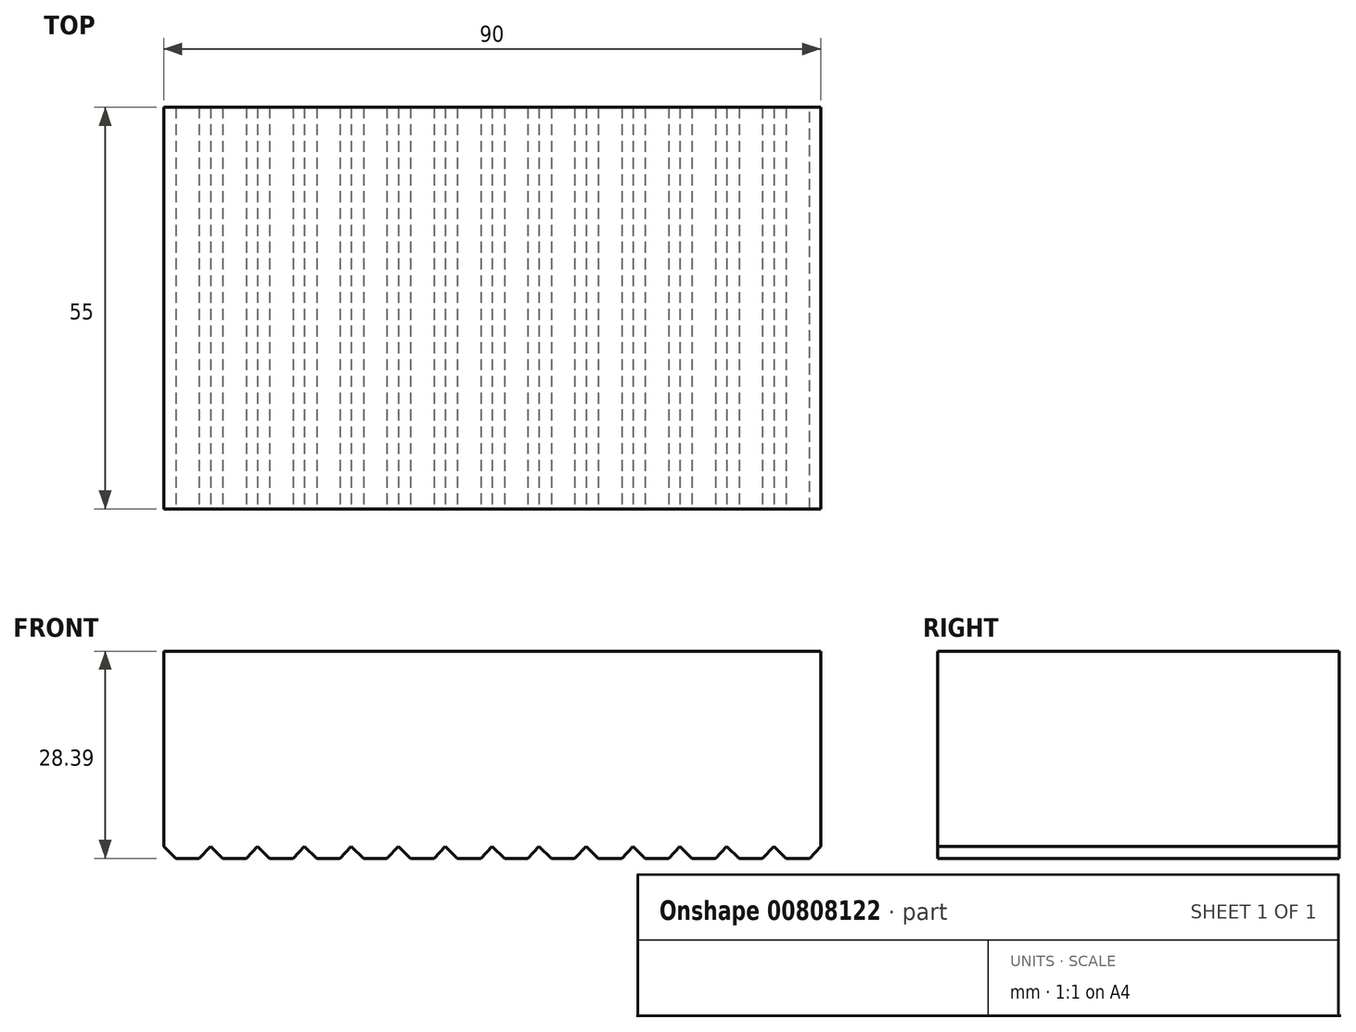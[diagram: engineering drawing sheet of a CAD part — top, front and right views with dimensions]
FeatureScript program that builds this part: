
annotation { "Feature Type Name" : "Feature", "Feature Type Description" : "" }
export const myFeature = defineFeature(function(context is Context, id is Id, definition is map)
    precondition{}
    {
        {
            var Q0;
            Q0=qCreatedBy(makeId("Top.planeOp"),FACE);
            var sketch = newSketch(context, id + "F0", { "sketchPlane" : qUnion([Q0])});
            skLineSegment(sketch, "E0.bottom", {"start": v(0, 0) * mm, "end": v(90, 0) * mm});
            skLineSegment(sketch, "E0.top", {"start": v(0, -55) * mm, "end": v(90, -55) * mm});
            skLineSegment(sketch, "E0.left", {"start": v(0, 0) * mm, "end": v(0, -55) * mm});
            skLineSegment(sketch, "E0.right", {"start": v(90, 0) * mm, "end": v(90, -55) * mm});
            skSolve(sketch);
        }
        {
            var Q0;
            Q0 = qSketchRegion(id + "F0", true);
            extrude(context, id + "F1", {"entities" : qUnion([Q0]), "depth" : 30 * mm, "offsetDistance" : 25 * mm});
        }
        {
            var Q0;
            Q0=makeQuery(id+"F1.opExtrude","SWEPT_FACE",FACE,{"disambiguationData":[OSD([sQuery(id+"F0.wireOp",EDGE,"E0.top")])]});
            var sketch = newSketch(context, id + "F2", { "sketchPlane" : qUnion([Q0])});
            skLineSegment(sketch, "E1", {"start": v(0, 3.21) * mm, "end": v(3.35, 0) * mm});
            skLineSegment(sketch, "E2", {"start": v(3.35, 0) * mm, "end": v(6.43, 3.21) * mm});
            skLineSegment(sketch, "E3", {"start": v(6.43, 3.21) * mm, "end": v(9.77, 0) * mm});
            skLineSegment(sketch, "E4", {"start": v(9.77, 0) * mm, "end": v(12.86, 3.21) * mm});
            skLineSegment(sketch, "E5", {"start": v(12.86, 3.21) * mm, "end": v(16.2, 0) * mm});
            skLineSegment(sketch, "E6", {"start": v(16.2, 0) * mm, "end": v(19.29, 3.21) * mm});
            skLineSegment(sketch, "E7", {"start": v(19.29, 3.21) * mm, "end": v(22.63, 0) * mm});
            skLineSegment(sketch, "E8", {"start": v(22.63, 0) * mm, "end": v(25.71, 3.21) * mm});
            skLineSegment(sketch, "E9", {"start": v(25.71, 3.21) * mm, "end": v(29.06, 0) * mm});
            skLineSegment(sketch, "E10", {"start": v(29.06, 0) * mm, "end": v(32.14, 3.21) * mm});
            skLineSegment(sketch, "E11", {"start": v(32.14, 3.21) * mm, "end": v(35.49, 0) * mm});
            skLineSegment(sketch, "E12", {"start": v(35.49, 0) * mm, "end": v(38.57, 3.21) * mm});
            skLineSegment(sketch, "E13", {"start": v(38.57, 3.21) * mm, "end": v(41.92, 0) * mm});
            skLineSegment(sketch, "E14", {"start": v(41.92, 0) * mm, "end": v(45, 3.21) * mm});
            skLineSegment(sketch, "E15", {"start": v(45, 3.21) * mm, "end": v(48.35, 0) * mm});
            skLineSegment(sketch, "E16", {"start": v(48.35, 0) * mm, "end": v(51.43, 3.21) * mm});
            skLineSegment(sketch, "E17", {"start": v(51.43, 3.21) * mm, "end": v(54.77, 0) * mm});
            skLineSegment(sketch, "E18", {"start": v(54.77, 0) * mm, "end": v(57.86, 3.21) * mm});
            skLineSegment(sketch, "E19", {"start": v(57.86, 3.21) * mm, "end": v(61.2, 0) * mm});
            skLineSegment(sketch, "E20", {"start": v(61.2, 0) * mm, "end": v(64.29, 3.21) * mm});
            skLineSegment(sketch, "E21", {"start": v(64.29, 3.21) * mm, "end": v(67.63, 0) * mm});
            skLineSegment(sketch, "E22", {"start": v(67.63, 0) * mm, "end": v(70.71, 3.21) * mm});
            skLineSegment(sketch, "E23", {"start": v(70.71, 3.21) * mm, "end": v(74.06, 0) * mm});
            skLineSegment(sketch, "E24", {"start": v(74.06, 0) * mm, "end": v(77.14, 3.21) * mm});
            skLineSegment(sketch, "E25", {"start": v(77.14, 3.21) * mm, "end": v(80.49, 0) * mm});
            skLineSegment(sketch, "E26", {"start": v(80.49, 0) * mm, "end": v(83.57, 3.21) * mm});
            skLineSegment(sketch, "E27", {"start": v(83.57, 3.21) * mm, "end": v(86.92, 0) * mm});
            skLineSegment(sketch, "E28", {"start": v(86.92, 0) * mm, "end": v(90, 3.21) * mm});
            skLineSegment(sketch, "E29", {"start": v(0, 3.21) * mm, "end": v(90, 3.21) * mm});
            skSolve(sketch);
        }
        {
            var Q0;
            {var subQ0=sQuery(id+"F2.wireOp",EDGE,"E1");Q0=makeQuery(id+"F2.imprint","IMPRINT",FACE,{"disambiguationData":[TD([[makeQuery(id+"F2.imprint","IMPRINT",EDGE,{"derivedFrom":subQ0}),-1.0]])]});}
            var Q1;
            {var subQ0=sQuery(id+"F2.wireOp",EDGE,"E2");Q1=makeQuery(id+"F2.imprint","IMPRINT",FACE,{"disambiguationData":[TD([[makeQuery(id+"F2.imprint","IMPRINT",EDGE,{"derivedFrom":subQ0}),-1.0]])]});}
            var Q2;
            {var subQ0=sQuery(id+"F2.wireOp",EDGE,"E4");Q2=makeQuery(id+"F2.imprint","IMPRINT",FACE,{"disambiguationData":[TD([[makeQuery(id+"F2.imprint","IMPRINT",EDGE,{"derivedFrom":subQ0}),-1.0]])]});}
            var Q3;
            {var subQ0=sQuery(id+"F2.wireOp",EDGE,"E6");Q3=makeQuery(id+"F2.imprint","IMPRINT",FACE,{"disambiguationData":[TD([[makeQuery(id+"F2.imprint","IMPRINT",EDGE,{"derivedFrom":subQ0}),-1.0]])]});}
            var Q4;
            {var subQ0=sQuery(id+"F2.wireOp",EDGE,"E8");Q4=makeQuery(id+"F2.imprint","IMPRINT",FACE,{"disambiguationData":[TD([[makeQuery(id+"F2.imprint","IMPRINT",EDGE,{"derivedFrom":subQ0}),-1.0]])]});}
            var Q5;
            {var subQ0=sQuery(id+"F2.wireOp",EDGE,"E10");Q5=makeQuery(id+"F2.imprint","IMPRINT",FACE,{"disambiguationData":[TD([[makeQuery(id+"F2.imprint","IMPRINT",EDGE,{"derivedFrom":subQ0}),-1.0]])]});}
            var Q6;
            {var subQ0=sQuery(id+"F2.wireOp",EDGE,"E12");Q6=makeQuery(id+"F2.imprint","IMPRINT",FACE,{"disambiguationData":[TD([[makeQuery(id+"F2.imprint","IMPRINT",EDGE,{"derivedFrom":subQ0}),-1.0]])]});}
            var Q7;
            {var subQ0=sQuery(id+"F2.wireOp",EDGE,"E14");Q7=makeQuery(id+"F2.imprint","IMPRINT",FACE,{"disambiguationData":[TD([[makeQuery(id+"F2.imprint","IMPRINT",EDGE,{"derivedFrom":subQ0}),-1.0]])]});}
            var Q8;
            {var subQ0=sQuery(id+"F2.wireOp",EDGE,"E16");Q8=makeQuery(id+"F2.imprint","IMPRINT",FACE,{"disambiguationData":[TD([[makeQuery(id+"F2.imprint","IMPRINT",EDGE,{"derivedFrom":subQ0}),-1.0]])]});}
            var Q9;
            {var subQ0=sQuery(id+"F2.wireOp",EDGE,"E18");Q9=makeQuery(id+"F2.imprint","IMPRINT",FACE,{"disambiguationData":[TD([[makeQuery(id+"F2.imprint","IMPRINT",EDGE,{"derivedFrom":subQ0}),-1.0]])]});}
            var Q10;
            {var subQ0=sQuery(id+"F2.wireOp",EDGE,"E20");Q10=makeQuery(id+"F2.imprint","IMPRINT",FACE,{"disambiguationData":[TD([[makeQuery(id+"F2.imprint","IMPRINT",EDGE,{"derivedFrom":subQ0}),-1.0]])]});}
            var Q11;
            {var subQ0=sQuery(id+"F2.wireOp",EDGE,"E22");Q11=makeQuery(id+"F2.imprint","IMPRINT",FACE,{"disambiguationData":[TD([[makeQuery(id+"F2.imprint","IMPRINT",EDGE,{"derivedFrom":subQ0}),-1.0]])]});}
            var Q12;
            {var subQ0=sQuery(id+"F2.wireOp",EDGE,"E24");Q12=makeQuery(id+"F2.imprint","IMPRINT",FACE,{"disambiguationData":[TD([[makeQuery(id+"F2.imprint","IMPRINT",EDGE,{"derivedFrom":subQ0}),-1.0]])]});}
            var Q13;
            {var subQ0=sQuery(id+"F2.wireOp",EDGE,"E26");Q13=makeQuery(id+"F2.imprint","IMPRINT",FACE,{"disambiguationData":[TD([[makeQuery(id+"F2.imprint","IMPRINT",EDGE,{"derivedFrom":subQ0}),-1.0]])]});}
            var Q14;
            {var subQ0=sQuery(id+"F2.wireOp",EDGE,"E28");Q14=makeQuery(id+"F2.imprint","IMPRINT",FACE,{"disambiguationData":[TD([[makeQuery(id+"F2.imprint","IMPRINT",EDGE,{"derivedFrom":subQ0}),-1.0]])]});}
            extrude(context, id + "F3", {"entities" : qUnion([Q0, Q1, Q2, Q3, Q4, Q5, Q6, Q7, Q8, Q9, Q10, Q11, Q12, Q13, Q14]), "operationType" : NewBodyOperationType.REMOVE, "oppositeDirection" : true, "depth" : 90 * mm, "offsetDistance" : 25 * mm});
        }
        {
            var Q0;
            Q0=makeQuery(id+"F1.opExtrude","SWEPT_FACE",FACE,{"disambiguationData":[OSD([sQuery(id+"F0.wireOp",EDGE,"E0.top")])]});
            var sketch = newSketch(context, id + "F4", { "sketchPlane" : qUnion([Q0])});
            skPoint(sketch, "E30.oppositeSnap0", {"position": v(88.46, 1.6) * mm});
            skLineSegment(sketch, "E30.bottom", {"start": v(0, 0) * mm, "end": v(90, 0) * mm});
            skLineSegment(sketch, "E30.top", {"start": v(0, 1.6) * mm, "end": v(90, 1.6) * mm});
            skLineSegment(sketch, "E30.left", {"start": v(0, 0) * mm, "end": v(0, 1.6) * mm});
            skLineSegment(sketch, "E30.right", {"start": v(90, 0) * mm, "end": v(90, 1.6) * mm});
            skSolve(sketch);
        }
        {
            var Q0;
            {var subQ3=sQuery(id+"F4.wireOp",EDGE,"E30.left");Q0=makeQuery(id+"F4.imprint","IMPRINT",FACE,{"disambiguationData":[TD([[makeQuery(id+"F4.imprint","IMPRINT",EDGE,{"derivedFrom":subQ3}),-1.0]])]});}
            var Q1;
            {var subQ3=sQuery(id+"F4.wireOp",EDGE,"E30.right");Q1=makeQuery(id+"F4.imprint","IMPRINT",FACE,{"disambiguationData":[TD([[makeQuery(id+"F4.imprint","IMPRINT",EDGE,{"derivedFrom":subQ3}),1.0]])]});}
            var Q2;
            {var subQ1=makeQuery(id+"F3.boolean.opBoolean","COPY",EDGE,{"derivedFrom":makeQuery(id+"F3.opExtrude","CAP_EDGE",EDGE,{"disambiguationData":[OSD([sQuery(id+"F2.wireOp",EDGE,"E2")])],"isStart":true})});var subQ5=sQuery(id+"F4.wireOp",EDGE,"E30.top");var subQ6=makeQuery(id+"F4.imprint","INTERSECT",VERTEX,{"derivedFrom":[subQ1,subQ5]});Q2=makeQuery(id+"F4.imprint","IMPRINT",FACE,{"disambiguationData":[TD([[makeQuery(id+"F4.imprint","IMPRINT",EDGE,{"disambiguationData":[TD([[subQ6,-1.0]])],"derivedFrom":subQ5}),-1.0]])]});}
            var Q3;
            {var subQ1=makeQuery(id+"F3.boolean.opBoolean","COPY",EDGE,{"derivedFrom":makeQuery(id+"F3.opExtrude","CAP_EDGE",EDGE,{"disambiguationData":[OSD([sQuery(id+"F2.wireOp",EDGE,"E4")])],"isStart":true})});var subQ5=sQuery(id+"F4.wireOp",EDGE,"E30.top");var subQ7=makeQuery(id+"F4.imprint","INTERSECT",VERTEX,{"derivedFrom":[subQ1,subQ5]});Q3=makeQuery(id+"F4.imprint","IMPRINT",FACE,{"disambiguationData":[TD([[makeQuery(id+"F4.imprint","IMPRINT",EDGE,{"disambiguationData":[TD([[subQ7,-1.0]])],"derivedFrom":subQ5}),-1.0]])]});}
            var Q4;
            {var subQ1=makeQuery(id+"F3.boolean.opBoolean","COPY",EDGE,{"derivedFrom":makeQuery(id+"F3.opExtrude","CAP_EDGE",EDGE,{"disambiguationData":[OSD([sQuery(id+"F2.wireOp",EDGE,"E8")])],"isStart":true})});var subQ5=sQuery(id+"F4.wireOp",EDGE,"E30.top");var subQ6=makeQuery(id+"F4.imprint","INTERSECT",VERTEX,{"derivedFrom":[subQ1,subQ5]});Q4=makeQuery(id+"F4.imprint","IMPRINT",FACE,{"disambiguationData":[TD([[makeQuery(id+"F4.imprint","IMPRINT",EDGE,{"disambiguationData":[TD([[subQ6,-1.0]])],"derivedFrom":subQ5}),-1.0]])]});}
            var Q5;
            {var subQ1=makeQuery(id+"F3.boolean.opBoolean","COPY",EDGE,{"derivedFrom":makeQuery(id+"F3.opExtrude","CAP_EDGE",EDGE,{"disambiguationData":[OSD([sQuery(id+"F2.wireOp",EDGE,"E10")])],"isStart":true})});var subQ5=sQuery(id+"F4.wireOp",EDGE,"E30.top");var subQ6=makeQuery(id+"F4.imprint","INTERSECT",VERTEX,{"derivedFrom":[subQ1,subQ5]});Q5=makeQuery(id+"F4.imprint","IMPRINT",FACE,{"disambiguationData":[TD([[makeQuery(id+"F4.imprint","IMPRINT",EDGE,{"disambiguationData":[TD([[subQ6,-1.0]])],"derivedFrom":subQ5}),-1.0]])]});}
            var Q6;
            {var subQ1=makeQuery(id+"F3.boolean.opBoolean","COPY",EDGE,{"derivedFrom":makeQuery(id+"F3.opExtrude","CAP_EDGE",EDGE,{"disambiguationData":[OSD([sQuery(id+"F2.wireOp",EDGE,"E12")])],"isStart":true})});var subQ5=sQuery(id+"F4.wireOp",EDGE,"E30.top");var subQ6=makeQuery(id+"F4.imprint","INTERSECT",VERTEX,{"derivedFrom":[subQ1,subQ5]});Q6=makeQuery(id+"F4.imprint","IMPRINT",FACE,{"disambiguationData":[TD([[makeQuery(id+"F4.imprint","IMPRINT",EDGE,{"disambiguationData":[TD([[subQ6,-1.0]])],"derivedFrom":subQ5}),-1.0]])]});}
            var Q7;
            {var subQ1=makeQuery(id+"F3.boolean.opBoolean","COPY",EDGE,{"derivedFrom":makeQuery(id+"F3.opExtrude","CAP_EDGE",EDGE,{"disambiguationData":[OSD([sQuery(id+"F2.wireOp",EDGE,"E14")])],"isStart":true})});var subQ5=sQuery(id+"F4.wireOp",EDGE,"E30.top");var subQ7=makeQuery(id+"F4.imprint","INTERSECT",VERTEX,{"derivedFrom":[subQ1,subQ5]});Q7=makeQuery(id+"F4.imprint","IMPRINT",FACE,{"disambiguationData":[TD([[makeQuery(id+"F4.imprint","IMPRINT",EDGE,{"disambiguationData":[TD([[subQ7,-1.0]])],"derivedFrom":subQ5}),-1.0]])]});}
            var Q8;
            {var subQ1=makeQuery(id+"F3.boolean.opBoolean","COPY",EDGE,{"derivedFrom":makeQuery(id+"F3.opExtrude","CAP_EDGE",EDGE,{"disambiguationData":[OSD([sQuery(id+"F2.wireOp",EDGE,"E16")])],"isStart":true})});var subQ5=sQuery(id+"F4.wireOp",EDGE,"E30.top");var subQ6=makeQuery(id+"F4.imprint","INTERSECT",VERTEX,{"derivedFrom":[subQ1,subQ5]});Q8=makeQuery(id+"F4.imprint","IMPRINT",FACE,{"disambiguationData":[TD([[makeQuery(id+"F4.imprint","IMPRINT",EDGE,{"disambiguationData":[TD([[subQ6,-1.0]])],"derivedFrom":subQ5}),-1.0]])]});}
            var Q9;
            {var subQ1=makeQuery(id+"F3.boolean.opBoolean","COPY",EDGE,{"derivedFrom":makeQuery(id+"F3.opExtrude","CAP_EDGE",EDGE,{"disambiguationData":[OSD([sQuery(id+"F2.wireOp",EDGE,"E18")])],"isStart":true})});var subQ5=sQuery(id+"F4.wireOp",EDGE,"E30.top");var subQ6=makeQuery(id+"F4.imprint","INTERSECT",VERTEX,{"derivedFrom":[subQ1,subQ5]});Q9=makeQuery(id+"F4.imprint","IMPRINT",FACE,{"disambiguationData":[TD([[makeQuery(id+"F4.imprint","IMPRINT",EDGE,{"disambiguationData":[TD([[subQ6,-1.0]])],"derivedFrom":subQ5}),-1.0]])]});}
            var Q10;
            {var subQ1=makeQuery(id+"F3.boolean.opBoolean","COPY",EDGE,{"derivedFrom":makeQuery(id+"F3.opExtrude","CAP_EDGE",EDGE,{"disambiguationData":[OSD([sQuery(id+"F2.wireOp",EDGE,"E20")])],"isStart":true})});var subQ5=sQuery(id+"F4.wireOp",EDGE,"E30.top");var subQ6=makeQuery(id+"F4.imprint","INTERSECT",VERTEX,{"derivedFrom":[subQ1,subQ5]});Q10=makeQuery(id+"F4.imprint","IMPRINT",FACE,{"disambiguationData":[TD([[makeQuery(id+"F4.imprint","IMPRINT",EDGE,{"disambiguationData":[TD([[subQ6,-1.0]])],"derivedFrom":subQ5}),-1.0]])]});}
            var Q11;
            {var subQ1=makeQuery(id+"F3.boolean.opBoolean","COPY",EDGE,{"derivedFrom":makeQuery(id+"F3.opExtrude","CAP_EDGE",EDGE,{"disambiguationData":[OSD([sQuery(id+"F2.wireOp",EDGE,"E22")])],"isStart":true})});var subQ5=sQuery(id+"F4.wireOp",EDGE,"E30.top");var subQ6=makeQuery(id+"F4.imprint","INTERSECT",VERTEX,{"derivedFrom":[subQ1,subQ5]});Q11=makeQuery(id+"F4.imprint","IMPRINT",FACE,{"disambiguationData":[TD([[makeQuery(id+"F4.imprint","IMPRINT",EDGE,{"disambiguationData":[TD([[subQ6,-1.0]])],"derivedFrom":subQ5}),-1.0]])]});}
            var Q12;
            {var subQ1=makeQuery(id+"F3.boolean.opBoolean","COPY",EDGE,{"derivedFrom":makeQuery(id+"F3.opExtrude","CAP_EDGE",EDGE,{"disambiguationData":[OSD([sQuery(id+"F2.wireOp",EDGE,"E24")])],"isStart":true})});var subQ5=sQuery(id+"F4.wireOp",EDGE,"E30.top");var subQ7=makeQuery(id+"F4.imprint","INTERSECT",VERTEX,{"derivedFrom":[subQ1,subQ5]});Q12=makeQuery(id+"F4.imprint","IMPRINT",FACE,{"disambiguationData":[TD([[makeQuery(id+"F4.imprint","IMPRINT",EDGE,{"disambiguationData":[TD([[subQ7,-1.0]])],"derivedFrom":subQ5}),-1.0]])]});}
            var Q13;
            {var subQ1=makeQuery(id+"F3.boolean.opBoolean","COPY",EDGE,{"derivedFrom":makeQuery(id+"F3.opExtrude","CAP_EDGE",EDGE,{"disambiguationData":[OSD([sQuery(id+"F2.wireOp",EDGE,"E26")])],"isStart":true})});var subQ5=sQuery(id+"F4.wireOp",EDGE,"E30.top");var subQ6=makeQuery(id+"F4.imprint","INTERSECT",VERTEX,{"derivedFrom":[subQ1,subQ5]});Q13=makeQuery(id+"F4.imprint","IMPRINT",FACE,{"disambiguationData":[TD([[makeQuery(id+"F4.imprint","IMPRINT",EDGE,{"disambiguationData":[TD([[subQ6,-1.0]])],"derivedFrom":subQ5}),-1.0]])]});}
            var Q14;
            {var subQ0=sQuery(id+"F4.wireOp",EDGE,"E30.top");var subQ1=makeQuery(id+"F3.boolean.opBoolean","COPY",EDGE,{"derivedFrom":makeQuery(id+"F3.opExtrude","CAP_EDGE",EDGE,{"disambiguationData":[OSD([sQuery(id+"F2.wireOp",EDGE,"E1")])],"isStart":true})});var subQ2=makeQuery(id+"F4.imprint","INTERSECT",VERTEX,{"derivedFrom":[subQ1,subQ0]});Q14=makeQuery(id+"F4.imprint","IMPRINT",FACE,{"disambiguationData":[TD([[makeQuery(id+"F4.imprint","IMPRINT",EDGE,{"disambiguationData":[TD([[subQ2,-1.0]])],"derivedFrom":subQ0}),-1.0]])]});}
            var Q15;
            {var subQ0=sQuery(id+"F4.wireOp",EDGE,"E30.top");var subQ1=makeQuery(id+"F3.boolean.opBoolean","COPY",EDGE,{"derivedFrom":makeQuery(id+"F3.opExtrude","CAP_EDGE",EDGE,{"disambiguationData":[OSD([sQuery(id+"F2.wireOp",EDGE,"E3")])],"isStart":true})});var subQ2=makeQuery(id+"F4.imprint","INTERSECT",VERTEX,{"derivedFrom":[subQ1,subQ0]});Q15=makeQuery(id+"F4.imprint","IMPRINT",FACE,{"disambiguationData":[TD([[makeQuery(id+"F4.imprint","IMPRINT",EDGE,{"disambiguationData":[TD([[subQ2,-1.0]])],"derivedFrom":subQ0}),-1.0]])]});}
            var Q16;
            {var subQ0=sQuery(id+"F4.wireOp",EDGE,"E30.top");var subQ1=makeQuery(id+"F3.boolean.opBoolean","COPY",EDGE,{"derivedFrom":makeQuery(id+"F3.opExtrude","CAP_EDGE",EDGE,{"disambiguationData":[OSD([sQuery(id+"F2.wireOp",EDGE,"E5")])],"isStart":true})});var subQ2=makeQuery(id+"F4.imprint","INTERSECT",VERTEX,{"derivedFrom":[subQ1,subQ0]});Q16=makeQuery(id+"F4.imprint","IMPRINT",FACE,{"disambiguationData":[TD([[makeQuery(id+"F4.imprint","IMPRINT",EDGE,{"disambiguationData":[TD([[subQ2,-1.0]])],"derivedFrom":subQ0}),-1.0]])]});}
            var Q17;
            {var subQ0=sQuery(id+"F4.wireOp",EDGE,"E30.top");var subQ1=makeQuery(id+"F3.boolean.opBoolean","COPY",EDGE,{"derivedFrom":makeQuery(id+"F3.opExtrude","CAP_EDGE",EDGE,{"disambiguationData":[OSD([sQuery(id+"F2.wireOp",EDGE,"E7")])],"isStart":true})});var subQ2=makeQuery(id+"F4.imprint","INTERSECT",VERTEX,{"derivedFrom":[subQ1,subQ0]});Q17=makeQuery(id+"F4.imprint","IMPRINT",FACE,{"disambiguationData":[TD([[makeQuery(id+"F4.imprint","IMPRINT",EDGE,{"disambiguationData":[TD([[subQ2,-1.0]])],"derivedFrom":subQ0}),-1.0]])]});}
            var Q18;
            {var subQ0=sQuery(id+"F4.wireOp",EDGE,"E30.top");var subQ1=makeQuery(id+"F3.boolean.opBoolean","COPY",EDGE,{"derivedFrom":makeQuery(id+"F3.opExtrude","CAP_EDGE",EDGE,{"disambiguationData":[OSD([sQuery(id+"F2.wireOp",EDGE,"E9")])],"isStart":true})});var subQ2=makeQuery(id+"F4.imprint","INTERSECT",VERTEX,{"derivedFrom":[subQ1,subQ0]});Q18=makeQuery(id+"F4.imprint","IMPRINT",FACE,{"disambiguationData":[TD([[makeQuery(id+"F4.imprint","IMPRINT",EDGE,{"disambiguationData":[TD([[subQ2,-1.0]])],"derivedFrom":subQ0}),-1.0]])]});}
            var Q19;
            {var subQ0=sQuery(id+"F4.wireOp",EDGE,"E30.top");var subQ1=makeQuery(id+"F3.boolean.opBoolean","COPY",EDGE,{"derivedFrom":makeQuery(id+"F3.opExtrude","CAP_EDGE",EDGE,{"disambiguationData":[OSD([sQuery(id+"F2.wireOp",EDGE,"E11")])],"isStart":true})});var subQ2=makeQuery(id+"F4.imprint","INTERSECT",VERTEX,{"derivedFrom":[subQ1,subQ0]});Q19=makeQuery(id+"F4.imprint","IMPRINT",FACE,{"disambiguationData":[TD([[makeQuery(id+"F4.imprint","IMPRINT",EDGE,{"disambiguationData":[TD([[subQ2,-1.0]])],"derivedFrom":subQ0}),-1.0]])]});}
            var Q20;
            {var subQ0=sQuery(id+"F4.wireOp",EDGE,"E30.top");var subQ1=makeQuery(id+"F3.boolean.opBoolean","COPY",EDGE,{"derivedFrom":makeQuery(id+"F3.opExtrude","CAP_EDGE",EDGE,{"disambiguationData":[OSD([sQuery(id+"F2.wireOp",EDGE,"E13")])],"isStart":true})});var subQ2=makeQuery(id+"F4.imprint","INTERSECT",VERTEX,{"derivedFrom":[subQ1,subQ0]});Q20=makeQuery(id+"F4.imprint","IMPRINT",FACE,{"disambiguationData":[TD([[makeQuery(id+"F4.imprint","IMPRINT",EDGE,{"disambiguationData":[TD([[subQ2,-1.0]])],"derivedFrom":subQ0}),-1.0]])]});}
            var Q21;
            {var subQ0=sQuery(id+"F4.wireOp",EDGE,"E30.top");var subQ1=makeQuery(id+"F3.boolean.opBoolean","COPY",EDGE,{"derivedFrom":makeQuery(id+"F3.opExtrude","CAP_EDGE",EDGE,{"disambiguationData":[OSD([sQuery(id+"F2.wireOp",EDGE,"E15")])],"isStart":true})});var subQ2=makeQuery(id+"F4.imprint","INTERSECT",VERTEX,{"derivedFrom":[subQ1,subQ0]});Q21=makeQuery(id+"F4.imprint","IMPRINT",FACE,{"disambiguationData":[TD([[makeQuery(id+"F4.imprint","IMPRINT",EDGE,{"disambiguationData":[TD([[subQ2,-1.0]])],"derivedFrom":subQ0}),-1.0]])]});}
            var Q22;
            {var subQ0=sQuery(id+"F4.wireOp",EDGE,"E30.top");var subQ1=makeQuery(id+"F3.boolean.opBoolean","COPY",EDGE,{"derivedFrom":makeQuery(id+"F3.opExtrude","CAP_EDGE",EDGE,{"disambiguationData":[OSD([sQuery(id+"F2.wireOp",EDGE,"E17")])],"isStart":true})});var subQ2=makeQuery(id+"F4.imprint","INTERSECT",VERTEX,{"derivedFrom":[subQ1,subQ0]});Q22=makeQuery(id+"F4.imprint","IMPRINT",FACE,{"disambiguationData":[TD([[makeQuery(id+"F4.imprint","IMPRINT",EDGE,{"disambiguationData":[TD([[subQ2,-1.0]])],"derivedFrom":subQ0}),-1.0]])]});}
            var Q23;
            {var subQ0=sQuery(id+"F4.wireOp",EDGE,"E30.top");var subQ1=makeQuery(id+"F3.boolean.opBoolean","COPY",EDGE,{"derivedFrom":makeQuery(id+"F3.opExtrude","CAP_EDGE",EDGE,{"disambiguationData":[OSD([sQuery(id+"F2.wireOp",EDGE,"E19")])],"isStart":true})});var subQ2=makeQuery(id+"F4.imprint","INTERSECT",VERTEX,{"derivedFrom":[subQ1,subQ0]});Q23=makeQuery(id+"F4.imprint","IMPRINT",FACE,{"disambiguationData":[TD([[makeQuery(id+"F4.imprint","IMPRINT",EDGE,{"disambiguationData":[TD([[subQ2,-1.0]])],"derivedFrom":subQ0}),-1.0]])]});}
            var Q24;
            {var subQ0=sQuery(id+"F4.wireOp",EDGE,"E30.top");var subQ1=makeQuery(id+"F3.boolean.opBoolean","COPY",EDGE,{"derivedFrom":makeQuery(id+"F3.opExtrude","CAP_EDGE",EDGE,{"disambiguationData":[OSD([sQuery(id+"F2.wireOp",EDGE,"E21")])],"isStart":true})});var subQ2=makeQuery(id+"F4.imprint","INTERSECT",VERTEX,{"derivedFrom":[subQ1,subQ0]});Q24=makeQuery(id+"F4.imprint","IMPRINT",FACE,{"disambiguationData":[TD([[makeQuery(id+"F4.imprint","IMPRINT",EDGE,{"disambiguationData":[TD([[subQ2,-1.0]])],"derivedFrom":subQ0}),-1.0]])]});}
            var Q25;
            {var subQ0=sQuery(id+"F4.wireOp",EDGE,"E30.top");var subQ1=makeQuery(id+"F3.boolean.opBoolean","COPY",EDGE,{"derivedFrom":makeQuery(id+"F3.opExtrude","CAP_EDGE",EDGE,{"disambiguationData":[OSD([sQuery(id+"F2.wireOp",EDGE,"E23")])],"isStart":true})});var subQ2=makeQuery(id+"F4.imprint","INTERSECT",VERTEX,{"derivedFrom":[subQ1,subQ0]});Q25=makeQuery(id+"F4.imprint","IMPRINT",FACE,{"disambiguationData":[TD([[makeQuery(id+"F4.imprint","IMPRINT",EDGE,{"disambiguationData":[TD([[subQ2,-1.0]])],"derivedFrom":subQ0}),-1.0]])]});}
            var Q26;
            {var subQ0=sQuery(id+"F4.wireOp",EDGE,"E30.top");var subQ1=makeQuery(id+"F3.boolean.opBoolean","COPY",EDGE,{"derivedFrom":makeQuery(id+"F3.opExtrude","CAP_EDGE",EDGE,{"disambiguationData":[OSD([sQuery(id+"F2.wireOp",EDGE,"E25")])],"isStart":true})});var subQ2=makeQuery(id+"F4.imprint","INTERSECT",VERTEX,{"derivedFrom":[subQ1,subQ0]});Q26=makeQuery(id+"F4.imprint","IMPRINT",FACE,{"disambiguationData":[TD([[makeQuery(id+"F4.imprint","IMPRINT",EDGE,{"disambiguationData":[TD([[subQ2,-1.0]])],"derivedFrom":subQ0}),-1.0]])]});}
            var Q27;
            {var subQ0=sQuery(id+"F4.wireOp",EDGE,"E30.top");var subQ1=makeQuery(id+"F3.boolean.opBoolean","COPY",EDGE,{"derivedFrom":makeQuery(id+"F3.opExtrude","CAP_EDGE",EDGE,{"disambiguationData":[OSD([sQuery(id+"F2.wireOp",EDGE,"E28")])],"isStart":true})});var subQ2=makeQuery(id+"F4.imprint","INTERSECT",VERTEX,{"derivedFrom":[subQ1,subQ0]});Q27=makeQuery(id+"F4.imprint","IMPRINT",FACE,{"disambiguationData":[TD([[makeQuery(id+"F4.imprint","IMPRINT",EDGE,{"disambiguationData":[TD([[subQ2,1.0]])],"derivedFrom":subQ0}),-1.0]])]});}
            extrude(context, id + "F5", {"entities" : qUnion([Q0, Q1, Q2, Q3, Q4, Q5, Q6, Q7, Q8, Q9, Q10, Q11, Q12, Q13, Q14, Q15, Q16, Q17, Q18, Q19, Q20, Q21, Q22, Q23, Q24, Q25, Q26, Q27]), "operationType" : NewBodyOperationType.REMOVE, "oppositeDirection" : true, "depth" : 60 * mm, "offsetDistance" : 25 * mm});
        }
    });
